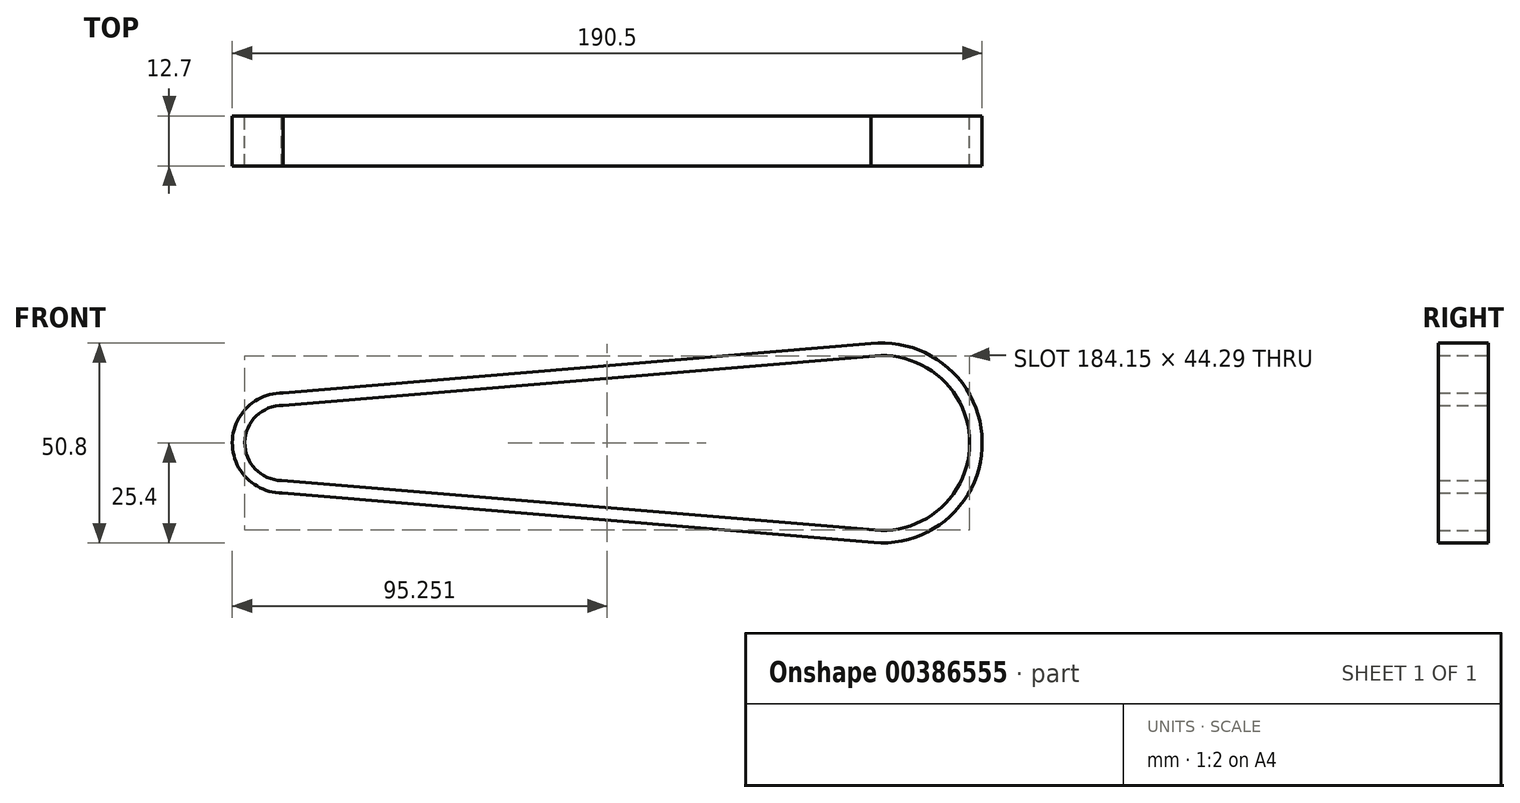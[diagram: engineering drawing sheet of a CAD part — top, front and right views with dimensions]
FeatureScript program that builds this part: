
annotation { "Feature Type Name" : "Feature", "Feature Type Description" : "" }
export const myFeature = defineFeature(function(context is Context, id is Id, definition is map)
    precondition{}
    {
        {
            var Q0;
            Q0=qCreatedBy(makeId("Front.planeOp"),FACE);
            var sketch = newSketch(context, id + "F0", { "sketchPlane" : qUnion([Q0])});
            skArc(sketch, "E0", {"start": v(-1.86, -22.15) * mm, "mid": v(22.22, 0) * mm, "end": v(-1.86, 22.15) * mm});
            skArc(sketch, "E1", {"start": v(-152.24, 9.52) * mm, "mid": v(-161.92, 0.17) * mm, "end": v(-152.58, -9.52) * mm});
            skLineSegment(sketch, "E2", {"start": v(-152.24, 9.52) * mm, "end": v(-1.86, 22.15) * mm});
            skLineSegment(sketch, "E3", {"start": v(-152.58, -9.52) * mm, "end": v(-1.86, -22.15) * mm});
            skArc(sketch, "E4", {"start": v(-14.11, -21.12) * mm, "mid": v(-14.11, -21.12) * mm, "end": v(-14.1, -21.12) * mm});
            skArc(sketch, "E5", {"start": v(-152.24, 12.7) * mm, "mid": v(-165.1, 0.1) * mm, "end": v(-152.42, -12.7) * mm});
            skLineSegment(sketch, "E6.MirrorCS", {"start": v(-152.24, -9.52) * mm, "end": v(-1.86, -22.15) * mm});
            skLineSegment(sketch, "E7", {"start": v(-152.24, 12.7) * mm, "end": v(-1.39, 25.36) * mm});
            skLineSegment(sketch, "E8", {"start": v(-152.42, -12.7) * mm, "end": v(-2.12, -25.31) * mm});
            skArc(sketch, "E9.trimOffspring", {"start": v(-144.8, -10.17) * mm, "mid": v(-144.78, -10.16) * mm, "end": v(-144.77, -10.15) * mm});
            skArc(sketch, "E10.trimOffspring", {"start": v(-2.12, -25.31) * mm, "mid": v(25.4, 0.37) * mm, "end": v(-2.86, 25.24) * mm});
            skSolve(sketch);
        }
        {
            var Q0;
            Q0 = qSketchRegion(id + "F0", true);
            extrude(context, id + "F1", {"entities" : qUnion([Q0]), "depth" : 12.7 * mm});
        }
    });
